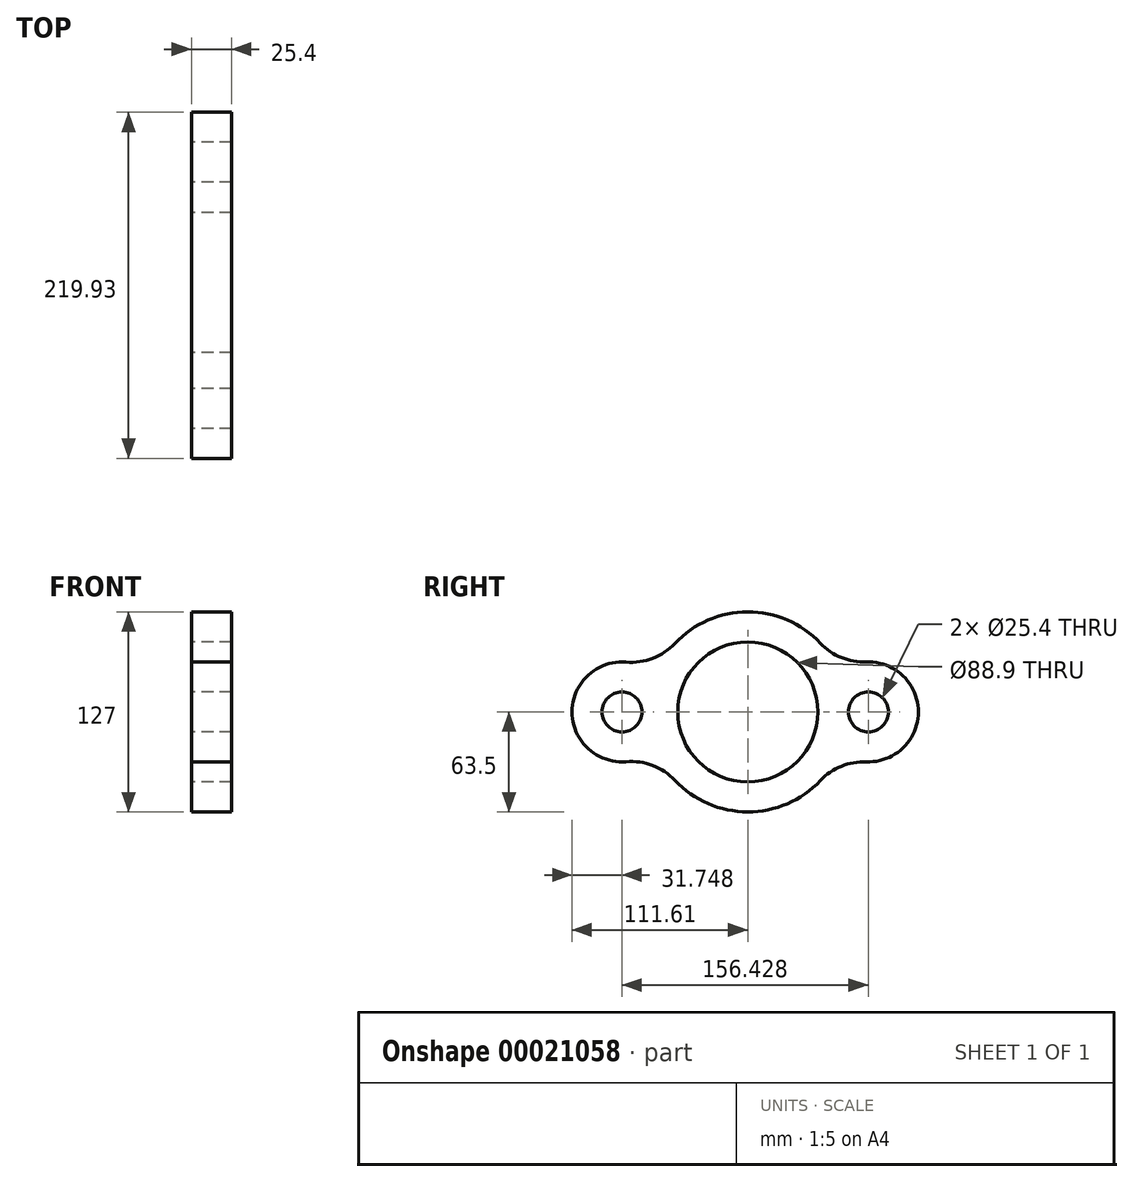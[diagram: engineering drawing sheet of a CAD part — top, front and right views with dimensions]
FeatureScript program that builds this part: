
annotation { "Feature Type Name" : "Feature", "Feature Type Description" : "" }
export const myFeature = defineFeature(function(context is Context, id is Id, definition is map)
    precondition{}
    {
        {
            var Q0;
            Q0=qCreatedBy(makeId("Right.planeOp"),FACE);
            var sketch = newSketch(context, id + "F0", { "sketchPlane" : qUnion([Q0])});
            skCircle(sketch, "E0", {"center": v(0, 0) * mm, "radius": 44.45 * mm});
            skArc(sketch, "E1", {"start": v(-46.26, -43.5) * mm, "mid": v(-0.08, -63.5) * mm, "end": v(46.14, -43.62) * mm});
            skLineSegment(sketch, "E2", {"start": v(-112.44, 0) * mm, "end": v(113.97, 0) * mm});
            skCircle(sketch, "E3", {"center": v(-79.86, 0) * mm, "radius": 12.7 * mm});
            skCircle(sketch, "E4", {"center": v(76.57, 0) * mm, "radius": 12.7 * mm});
            skArc(sketch, "E5", {"start": v(-77.2, 31.64) * mm, "mid": v(-111.61, 0) * mm, "end": v(-77.2, -31.64) * mm});
            skArc(sketch, "E6", {"start": v(75.32, -31.73) * mm, "mid": v(108.32, 0) * mm, "end": v(75.32, 31.73) * mm});
            skArc(sketch, "E7.trimOffspring", {"start": v(46.14, 43.62) * mm, "mid": v(-0.08, 63.5) * mm, "end": v(-46.26, 43.5) * mm});
            skPoint(sketch, "E8.visualSharp", {"position": v(58.03, 25.78) * mm});
            skArc(sketch, "E8.filletArc", {"start": v(46.14, 43.62) * mm, "mid": v(59.45, 34.52) * mm, "end": v(75.32, 31.73) * mm});
            skPoint(sketch, "E9.visualSharp", {"position": v(-58.86, -23.82) * mm});
            skArc(sketch, "E9.filletArc", {"start": v(-46.26, -43.5) * mm, "mid": v(-60.37, -34.03) * mm, "end": v(-77.2, -31.64) * mm});
            skPoint(sketch, "E10.visualSharp", {"position": v(58.03, -25.78) * mm});
            skArc(sketch, "E10.filletArc", {"start": v(75.32, -31.73) * mm, "mid": v(59.45, -34.52) * mm, "end": v(46.14, -43.62) * mm});
            skPoint(sketch, "E11.visualSharp", {"position": v(-58.86, 23.82) * mm});
            skArc(sketch, "E11.filletArc", {"start": v(-77.2, 31.64) * mm, "mid": v(-60.37, 34.03) * mm, "end": v(-46.26, 43.5) * mm});
            skSolve(sketch);
        }
        {
            var Q0;
            Q0 = qSketchRegion(id + "F0", true);
            extrude(context, id + "F1", {"entities" : qUnion([Q0]), "depth" : 25.4 * mm});
        }
    });
